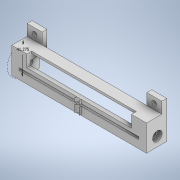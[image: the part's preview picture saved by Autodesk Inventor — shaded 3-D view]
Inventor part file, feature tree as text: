
AUTODESK INVENTOR PART (.ipt)
format: ipt  version: 2020 (Build 240168000, 168)  size: 485,376 bytes
history: native  units: mm
features: sketch x22, extrude x15, fillet x1
ambient origin geometry x8: Origin, YZ Plane, XZ Plane, XY Plane, X Axis, Y Axis, Z Axis, Center Point
bodies: Solid1 (feature_tree)
feature tree (38):
  extrude  "Extrusion1"  Depth=27.0mm
  extrude  "Extrusion2"  Depth=25.0mm
  sketch  "Sketch3"  dims[d4=10.0mm d5=0.0mm d6=10.0mm]
  sketch  "Sketch4"  dims[d7=10.0mm d8=0.0mm d9=5.0mm]
  sketch  "Sketch5"  dims[d10=11.0mm d11=5.0mm]
  extrude  "Extrusion3"  Depth=10.0mm
  extrude  "Extrusion4"  Depth=5.0mm
  extrude  "Extrusion5"  Depth=5.0mm
  extrude  "Extrusion6"  Depth=10.0mm
  fillet  "Fillet1"  Radius=7.5mm
  extrude  "Extrusion7"  Depth=10.0mm TaperAngle=0.0deg
  sketch  "Sketch11"  dims[d28=3.0mm d29=12.0mm]
  extrude  "Extrusion8"  Depth=7.0mm
  sketch  "Sketch13"  dims[d33=41.275mm d34=7.0mm]
  extrude  "Extrusion9"  Depth=3.0mm
  extrude  "Extrusion10"  Depth=12.0mm
  sketch  "Sketch16"  dims[d42=2.0mm]
  extrude  "Extrusion11"  Depth=12.0mm
  sketch  "Sketch18"  dims[d45=15.0mm d46=0.0mm]
  extrude  "Extrusion12"  Depth=23.5mm TaperAngle=0.0deg
  extrude  "Extrusion13"  Depth=7.0mm
  extrude  "Extrusion14"  Depth=7.0mm
  extrude  "Extrusion15"  Depth=19.0mm TaperAngle=0.0deg
  sketch  "Sketch1"  dims[d0=35.0mm d1=27.0mm]
  sketch  "Sketch2"  dims[d2=25.0mm d3=12.7mm]
  sketch  "Sketch6"  dims[d12=150.0mm d13=0.0mm d14=10.0mm d15=7.5mm d16=0.0mm]
  sketch  "Sketch7"  dims[d17=10.0mm d18=0.0mm d19=10.0mm d20=0.0mm]
  sketch  "Sketch8"  dims[d21=2.0mm d22=7.0mm]
  sketch  "Sketch9"  dims[d23=14.0mm d24=3.0mm]
  sketch  "Sketch10"  dims[d25=140.0mm d26=0.0mm d27=12.0mm]
  sketch  "Sketch12"  dims[d30=3.0mm d31=23.5mm d32=0.0mm]
  sketch  "Sketch14"  dims[d35=4.5mm d36=0.0mm d37=7.0mm]
  sketch  "Sketch15"  dims[d38=4.5mm d39=0.0mm d40=19.0mm d41=0.0mm]
  sketch  "Sketch17"  dims[d43=19.0mm d44=0.0mm]
  sketch  "Sketch19"  dims[d47=6.4mm]
  sketch  "Sketch20"  dims[d48=15.0mm d49=0.0mm]
  sketch  "Sketch21"  dims[d50=20.0mm]
  sketch  "Sketch22"  dims[d51=15.0mm d52=6.4mm d53=6.5mm d54=0.0mm]
